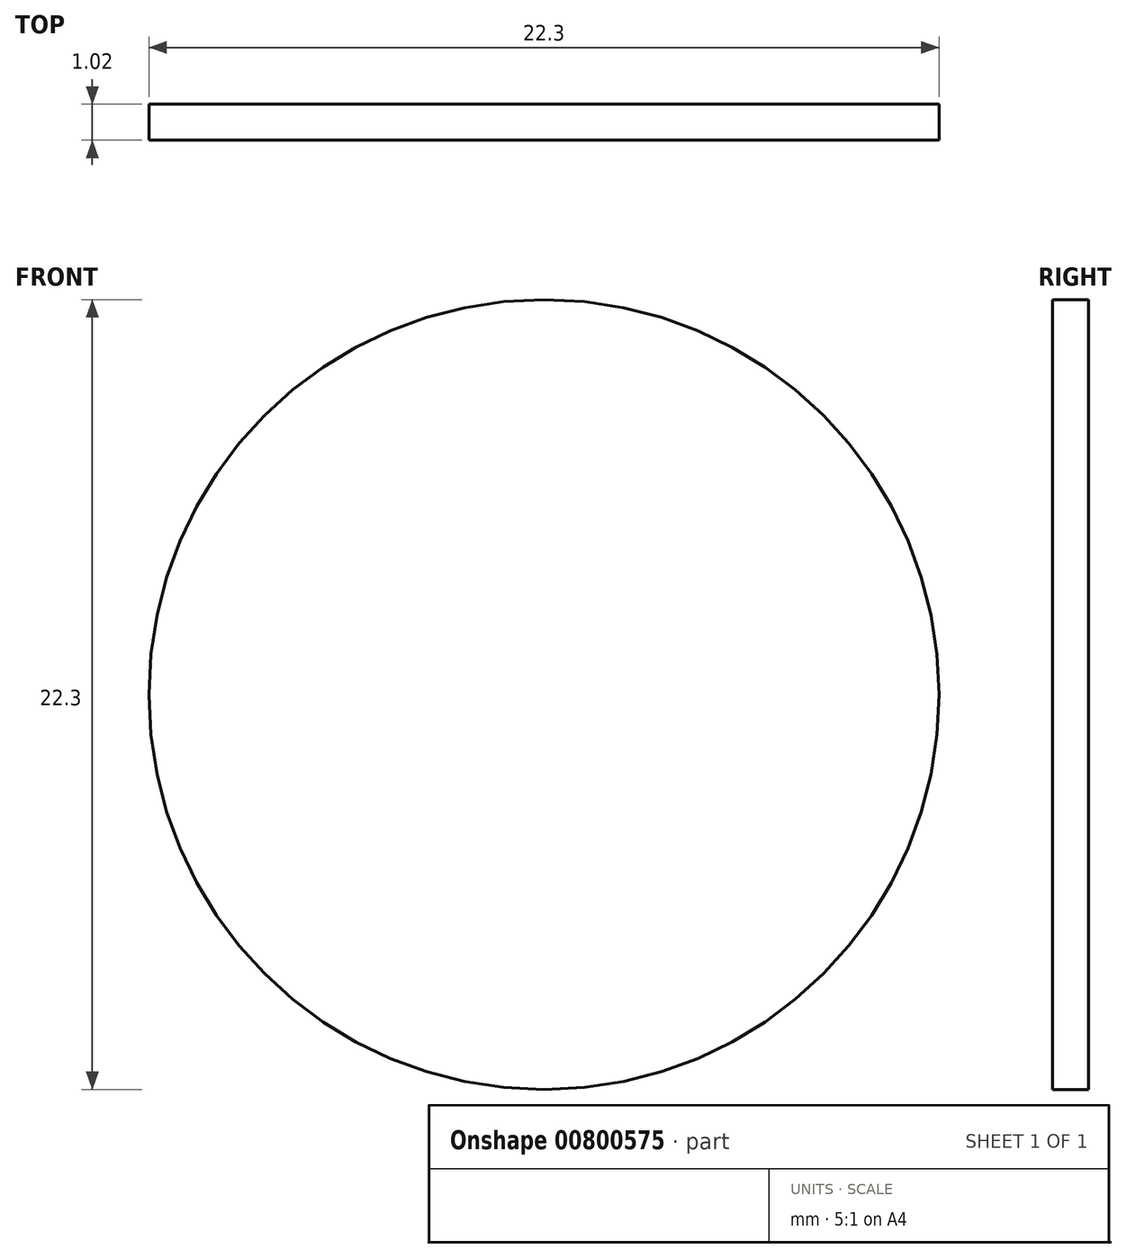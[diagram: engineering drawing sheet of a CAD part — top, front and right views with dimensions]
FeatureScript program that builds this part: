
annotation { "Feature Type Name" : "Feature", "Feature Type Description" : "" }
export const myFeature = defineFeature(function(context is Context, id is Id, definition is map)
    precondition{}
    {
        {
            var Q0;
            Q0=qCreatedBy(makeId("Front.planeOp"),FACE);
            var sketch = newSketch(context, id + "F0", { "sketchPlane" : qUnion([Q0])});
            skCircle(sketch, "E0", {"center": v(0, 0) * mm, "radius": 11.15 * mm});
            skSolve(sketch);
        }
        {
            var Q0;
            Q0=makeQuery(id+"F0.imprint","IMPRINT",FACE,{"disambiguationData":[TD([[makeQuery(id+"F0.imprint","IMPRINT",EDGE,{"derivedFrom":sQuery(id+"F0.wireOp",EDGE,"E0")}),1.0]])]});
            var Q1;
            Q1=sQuery(id+"F0.wireOp",EDGE,"E0");
            extrude(context, id + "F1", {"entities" : qUnion([Q0]), "surfaceEntities" : qUnion([Q1]), "depth" : 1.02 * mm, "offsetDistance" : 25.4 * mm});
        }
    });
